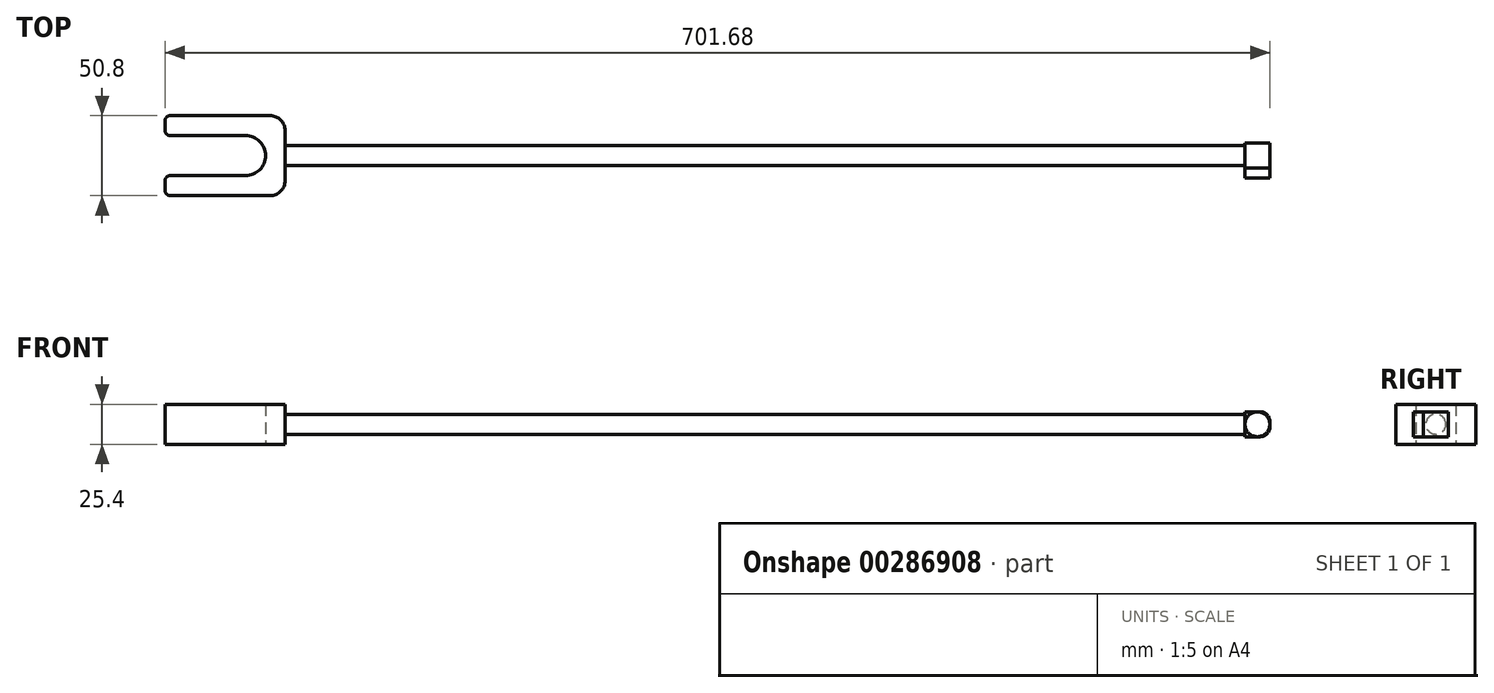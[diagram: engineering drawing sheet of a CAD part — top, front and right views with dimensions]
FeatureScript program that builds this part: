
annotation { "Feature Type Name" : "Feature", "Feature Type Description" : "" }
export const myFeature = defineFeature(function(context is Context, id is Id, definition is map)
    precondition{}
    {
        {
            var Q0;
            Q0=qCreatedBy(makeId("Right.planeOp"),FACE);
            var sketch = newSketch(context, id + "F0", { "sketchPlane" : qUnion([Q0])});
            skCircle(sketch, "E0", {"center": v(0, 0) * mm, "radius": 6.35 * mm});
            skSolve(sketch);
        }
        {
            var Q0;
            Q0 = qSketchRegion(id + "F0", true);
            extrude(context, id + "F1", {"entities" : qUnion([Q0]), "oppositeDirection" : true, "depth" : 609.6 * mm});
        }
        {
            var Q0;
            Q0=qCreatedBy(makeId("Right.planeOp"),FACE);
            var sketch = newSketch(context, id + "F2", { "sketchPlane" : qUnion([Q0])});
            skLineSegment(sketch, "E1.bottom", {"start": v(-7.94, 7.94) * mm, "end": v(7.94, 7.94) * mm});
            skLineSegment(sketch, "E1.top", {"start": v(-7.94, -7.94) * mm, "end": v(7.94, -7.94) * mm});
            skLineSegment(sketch, "E1.left", {"start": v(-7.94, 7.94) * mm, "end": v(-7.94, -7.94) * mm});
            skLineSegment(sketch, "E1.right", {"start": v(7.94, 7.94) * mm, "end": v(7.94, -7.94) * mm});
            skSolve(sketch);
        }
        {
            var Q0;
            Q0 = qSketchRegion(id + "F2", true);
            extrude(context, id + "F3", {"entities" : qUnion([Q0]), "operationType" : NewBodyOperationType.ADD, "depth" : 15.88 * mm});
        }
        {
            var Q0;
            Q0=makeQuery(id+"F3.opExtrude","SWEPT_FACE",FACE,{"disambiguationData":[OSD([sQuery(id+"F2.wireOp",EDGE,"E1.left")])]});
            var sketch = newSketch(context, id + "F4", { "sketchPlane" : qUnion([Q0])});
            skCircle(sketch, "E2", {"center": v(7.94, 0) * mm, "radius": 7.94 * mm});
            skPoint(sketch, "E2.first.point", {"position": v(15.88, 0) * mm});
            skPoint(sketch, "E2.second.point", {"position": v(0, 0) * mm});
            skPoint(sketch, "E2.third.point", {"position": v(7.94, -7.94) * mm});
            skSolve(sketch);
        }
        {
            var Q0;
            Q0 = qSketchRegion(id + "F4", true);
            extrude(context, id + "F5", {"entities" : qUnion([Q0]), "operationType" : NewBodyOperationType.ADD, "depth" : 6.35 * mm});
        }
        {
            var Q0;
            Q0=makeQuery(id+"F3.opExtrude","CAP_EDGE",EDGE,{"disambiguationData":[OSD([sQuery(id+"F2.wireOp",EDGE,"E1.bottom")])],"isStart":false});
            var Q1;
            Q1=makeQuery(id+"F3.opExtrude","CAP_EDGE",EDGE,{"disambiguationData":[OSD([sQuery(id+"F2.wireOp",EDGE,"E1.top")])],"isStart":false});
            fillet(context, id + "F6", {"entities" : qUnion([Q0, Q1]), "radius" : 6.35 * mm, "tangentPropagation" : true, "allowEdgeOverflow" : false});
        }
        {
            var Q0;
            Q0=qCreatedBy(makeId("Top.planeOp"),FACE);
            var sketch = newSketch(context, id + "F7", { "sketchPlane" : qUnion([Q0])});
            skLineSegment(sketch, "E3.bottom", {"start": v(-609.6, 25.4) * mm, "end": v(-685.8, 25.4) * mm});
            skLineSegment(sketch, "E3.top", {"start": v(-609.6, -25.4) * mm, "end": v(-685.8, -25.4) * mm});
            skLineSegment(sketch, "E3.left", {"start": v(-609.6, 25.4) * mm, "end": v(-609.6, -25.4) * mm});
            skLineSegment(sketch, "E3.right", {"start": v(-685.8, 25.4) * mm, "end": v(-685.8, -25.4) * mm});
            skLineSegment(sketch, "E4.bottom", {"start": v(-685.8, 12.7) * mm, "end": v(-634.73, 12.7) * mm});
            skLineSegment(sketch, "E4.top", {"start": v(-685.8, -12.7) * mm, "end": v(-634.73, -12.7) * mm});
            skLineSegment(sketch, "E4.left", {"start": v(-685.8, 12.7) * mm, "end": v(-685.8, -12.7) * mm});
            skLineSegment(sketch, "E4.right", {"start": v(-634.73, 12.7) * mm, "end": v(-634.73, -12.7) * mm});
            skArc(sketch, "E5", {"start": v(-634.73, -12.7) * mm, "mid": v(-622.03, 0) * mm, "end": v(-634.73, 12.7) * mm});
            skSolve(sketch);
        }
        {
            var Q0;
            {var subQ1=sQuery(id+"F7.wireOp",EDGE,"E3.bottom");Q0=makeQuery(id+"F7.imprint","IMPRINT",FACE,{"disambiguationData":[TD([[makeQuery(id+"F7.imprint","IMPRINT",EDGE,{"derivedFrom":subQ1}),1.0]])]});}
            extrude(context, id + "F8", {"entities" : qUnion([Q0]), "operationType" : NewBodyOperationType.ADD, "depth" : 25.4 * mm, "symmetric" : true});
        }
        {
            var Q0;
            Q0=makeQuery(id+"F8.opExtrude","SWEPT_EDGE",EDGE,{"disambiguationData":[OSD([sQuery(id+"F7.wireOp",EDGE,"E3.bottom"),sQuery(id+"F7.wireOp",EDGE,"E3.left")])]});
            var Q1;
            Q1=makeQuery(id+"F8.opExtrude","SWEPT_EDGE",EDGE,{"disambiguationData":[OSD([sQuery(id+"F7.wireOp",EDGE,"E3.top"),sQuery(id+"F7.wireOp",EDGE,"E3.left")])]});
            fillet(context, id + "F9", {"entities" : qUnion([Q0, Q1]), "radius" : 9.52 * mm, "tangentPropagation" : true, "allowEdgeOverflow" : false});
        }
        {
            var Q0;
            Q0=makeQuery(id+"F8.opExtrude","SWEPT_EDGE",EDGE,{"disambiguationData":[OSD([sQuery(id+"F7.wireOp",EDGE,"E3.bottom"),sQuery(id+"F7.wireOp",EDGE,"E3.right")])]});
            var Q1;
            Q1=makeQuery(id+"F8.opExtrude","SWEPT_EDGE",EDGE,{"disambiguationData":[OSD([sQuery(id+"F7.wireOp",EDGE,"E3.top"),sQuery(id+"F7.wireOp",EDGE,"E3.right")])]});
            var Q2;
            Q2=makeQuery(id+"F8.opExtrude","SWEPT_EDGE",EDGE,{"disambiguationData":[OSD([sQuery(id+"F7.wireOp",EDGE,"E3.right"),sQuery(id+"F7.wireOp",EDGE,"E4.bottom"),sQuery(id+"F7.wireOp",EDGE,"E4.left")])]});
            var Q3;
            Q3=makeQuery(id+"F8.opExtrude","SWEPT_EDGE",EDGE,{"disambiguationData":[OSD([sQuery(id+"F7.wireOp",EDGE,"E3.right"),sQuery(id+"F7.wireOp",EDGE,"E4.top"),sQuery(id+"F7.wireOp",EDGE,"E4.left")])]});
            fillet(context, id + "F10", {"entities" : qUnion([Q0, Q1, Q2, Q3]), "radius" : 3.17 * mm, "tangentPropagation" : true, "allowEdgeOverflow" : false});
        }
    });
